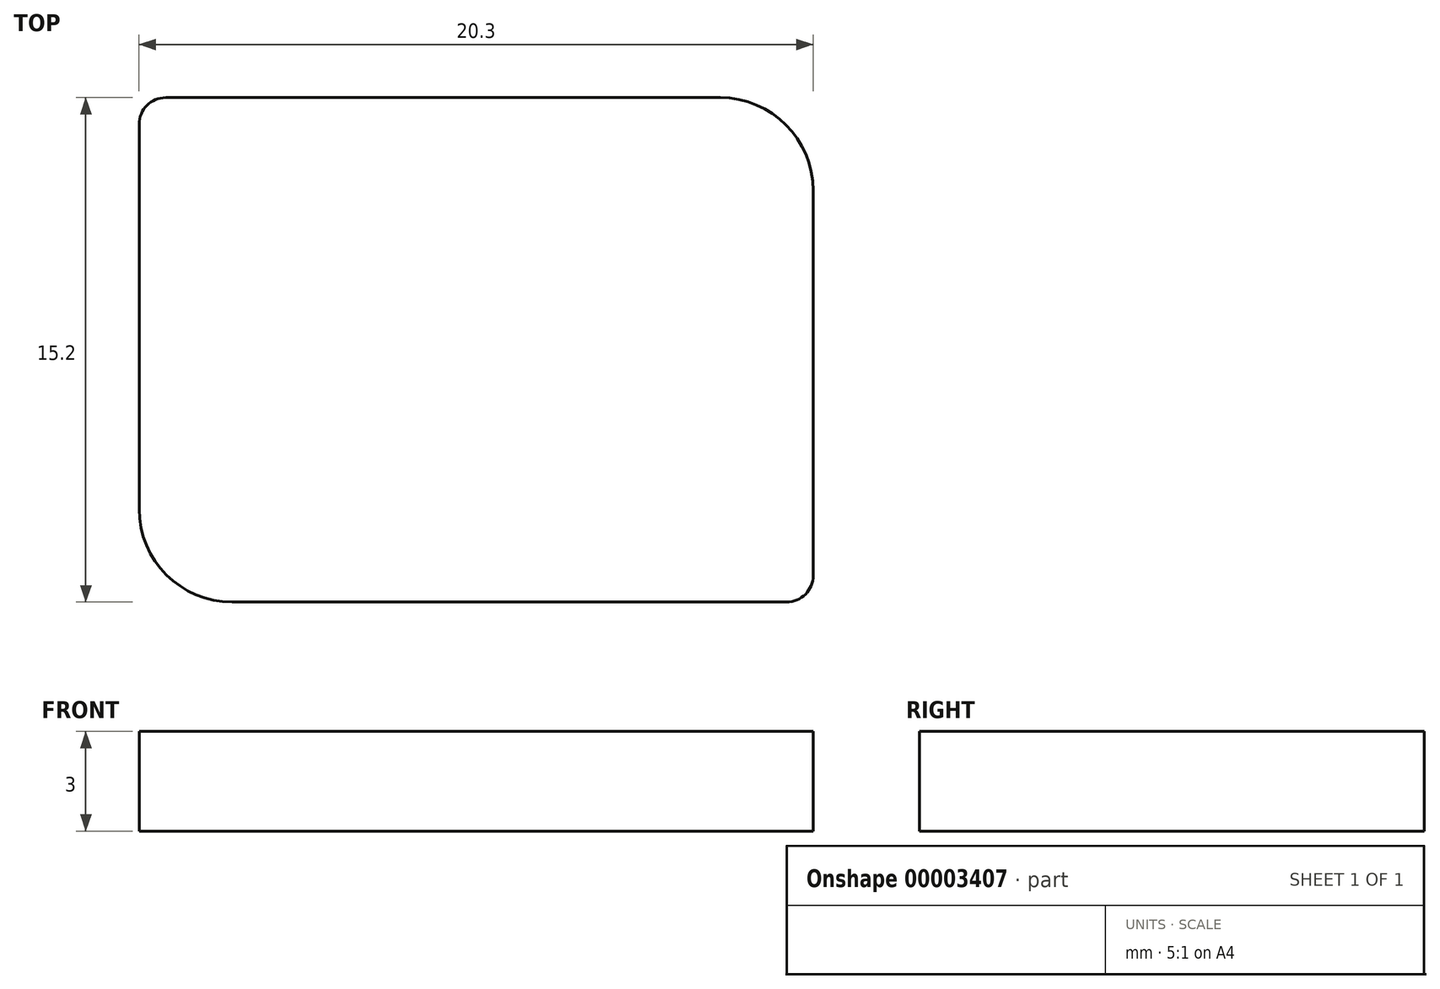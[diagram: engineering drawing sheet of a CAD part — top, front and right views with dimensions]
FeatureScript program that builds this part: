
annotation { "Feature Type Name" : "Feature", "Feature Type Description" : "" }
export const myFeature = defineFeature(function(context is Context, id is Id, definition is map)
    precondition{}
    {
        {
            var Q0;
            Q0=qCreatedBy(makeId("Top.planeOp"),FACE);
            var sketch = newSketch(context, id + "F0", { "sketchPlane" : qUnion([Q0])});
            skLineSegment(sketch, "E0.bottom", {"start": v(-50.1, -23.52) * mm, "end": v(-33.4, -23.52) * mm});
            skLineSegment(sketch, "E0.top", {"start": v(-48.1, -38.72) * mm, "end": v(-31.4, -38.72) * mm});
            skLineSegment(sketch, "E0.left", {"start": v(-50.9, -24.32) * mm, "end": v(-50.9, -35.92) * mm});
            skLineSegment(sketch, "E0.right", {"start": v(-30.6, -26.32) * mm, "end": v(-30.6, -37.92) * mm});
            skPoint(sketch, "E1.visualSharp", {"position": v(-50.9, -23.52) * mm});
            skArc(sketch, "E1.filletArc", {"start": v(-50.1, -23.52) * mm, "mid": v(-50.67, -23.75) * mm, "end": v(-50.9, -24.32) * mm});
            skPoint(sketch, "E2.visualSharp", {"position": v(-30.6, -38.72) * mm});
            skArc(sketch, "E2.filletArc", {"start": v(-31.4, -38.72) * mm, "mid": v(-30.84, -38.48) * mm, "end": v(-30.6, -37.92) * mm});
            skPoint(sketch, "E3.visualSharp", {"position": v(-30.6, -23.52) * mm});
            skArc(sketch, "E3.filletArc", {"start": v(-30.6, -26.32) * mm, "mid": v(-31.43, -24.34) * mm, "end": v(-33.4, -23.52) * mm});
            skPoint(sketch, "E4.visualSharp", {"position": v(-50.9, -38.72) * mm});
            skArc(sketch, "E4.filletArc", {"start": v(-50.9, -35.92) * mm, "mid": v(-50.09, -37.9) * mm, "end": v(-48.1, -38.72) * mm});
            skSolve(sketch);
        }
        {
            var Q0;
            Q0=makeQuery(id+"F0.imprint","IMPRINT",FACE,{"disambiguationData":[TD([[makeQuery(id+"F0.imprint","IMPRINT",EDGE,{"derivedFrom":sQuery(id+"F0.wireOp",EDGE,"E0.bottom")}),-1.0]])]});
            extrude(context, id + "F1", {"entities" : qUnion([Q0]), "depth" : 3 * mm});
        }
    });
